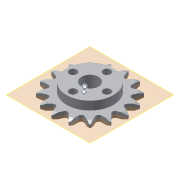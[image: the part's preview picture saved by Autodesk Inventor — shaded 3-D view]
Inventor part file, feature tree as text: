
AUTODESK INVENTOR PART (.ipt)
format: ipt  version: 2013 (Build 170138000, 138)  size: 413,184 bytes
history: native  units: in
note: dims shown in document units (in); Inventor stores cm internally (conversion verified against a paired STEP export)
features: other x17, plane x1
ambient origin geometry x8: Origin, YZ Plane, XZ Plane, XY Plane, X Axis, Y Axis, Z Axis, Center Point
bodies: Solid1 (feature_tree)
feature tree (18):
  other  "Tetrix sprocket 16T.ipt"
  other  "sprocket_25_16t_tetrix::Tetrix sprocket 16T.ipt"
  other  "TaggingFeature1"
  other  "FRONT"
  other  "TOP"
  other  "RIGHT"
  plane  "Work Plane4"
  other  "A_1"
  other  "A_2"
  other  "A_4"
  other  "A_5"
  other  "A_6"
  other  "A_3"
  other  "A_7"
  other  "A_8"
  other  "A_9"
  other  "iComposite:2"
  other  "iComposite:1"
